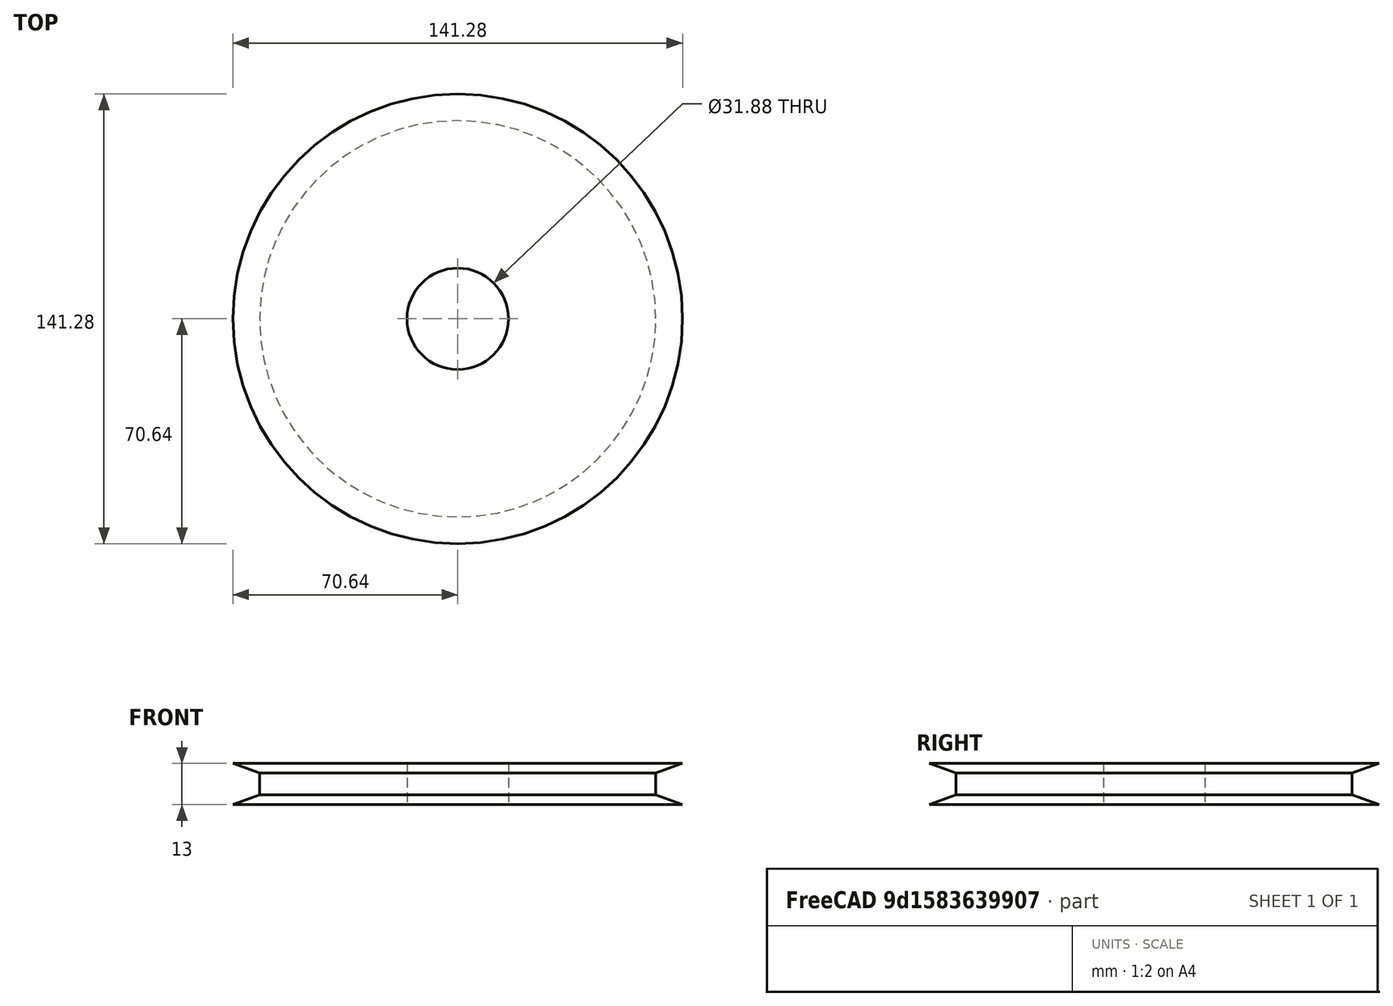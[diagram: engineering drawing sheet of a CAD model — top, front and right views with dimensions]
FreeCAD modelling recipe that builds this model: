
FCSTD DOCUMENT  (FreeCAD 0.18R16110 (Git))
Label: yvespulley
License: All rights reserved
LicenseURL: http://en.wikipedia.org/wiki/All_rights_reserved
objects: Sketcher::SketchObject×1, PartDesign::Revolution×1, PartDesign::Body×1
note: 4 computed .brp shape members not serialized (recipe doc carries the construction recipe); baked Part::Feature solids carry a one-line shape summary decoded from their .brp

FEATURE [Sketcher::SketchObject] Sketch
  MapMode = 5
  Placement = pos=(0,0,0) rot=(1,0,0;1.5708rad)
  Support = -> [XZ_Plane]
  sketch-geometry (8):
    g0: LineSegment StartX=15.9377 StartY=6.5 StartZ=0 EndX=15.9377 EndY=-6.5 EndZ=0
    g1: LineSegment StartX=15.9377 StartY=6.5 StartZ=0 EndX=70.6377 EndY=6.5 EndZ=0
    g2: LineSegment StartX=15.9377 StartY=-6.5 StartZ=0 EndX=70.6377 EndY=-6.5 EndZ=0
    g3: LineSegment StartX=70.6377 StartY=6.5 StartZ=0 EndX=62.2377 EndY=3.44265 EndZ=0
    g4: LineSegment StartX=70.6377 StartY=-6.5 StartZ=0 EndX=62.2377 EndY=-3.44265 EndZ=0
    g5: LineSegment [constr] StartX=70.6377 StartY=6.5 StartZ=0 EndX=70.6377 EndY=-6.5 EndZ=0
    g6: LineSegment [constr] StartX=70.6377 StartY=0 StartZ=0 EndX=62.2377 EndY=0 EndZ=0
    g7: LineSegment StartX=62.2377 StartY=3.44265 StartZ=0 EndX=62.2377 EndY=-3.44265 EndZ=0
  constraints (22):
    c: Symmetric(g0,g0,g-1)
    c: DistanceY(g0,g0) = 13
    c: Coincident(g1,g0)
    c: Horizontal(g1)
    c: Coincident(g2,g0)
    c: Horizontal(g2)
    c: Equal(g2,g1)
    c: Distance(g1) = 54.7
    c: Coincident(g3,g1)
    c: Coincident(g4,g2)
    c: Equal(g4,g3)
    c: Angle(g4,g3) = 0.698132
    c: Coincident(g5,g1)
    c: Coincident(g5,g2)
    c: PointOnObject(g6,g5)
    c: PointOnObject(g6,g-1)
    c: Horizontal(g6)
    c: Coincident(g7,g3)
    c: Coincident(g7,g4)
    c: Vertical(g7)
    c: PointOnObject(g6,g7)
    c: Distance(g6) = 8.4
FEATURE [PartDesign::Revolution] Revolution
  Angle = 360
  Axis = (0,-2e-16,1)
  Base = (0,0,0)
  Placement = pos=(0,0,0) rot=(1,0,0;1.5708rad)
  Profile = -> Sketch
  ReferenceAxis = -> Sketch [V_Axis]
  Reversed = true
FEATURE [PartDesign::Body] Body
  Group = -> [Sketch,Revolution]
  Origin = -> Origin
  Tip = -> Revolution
